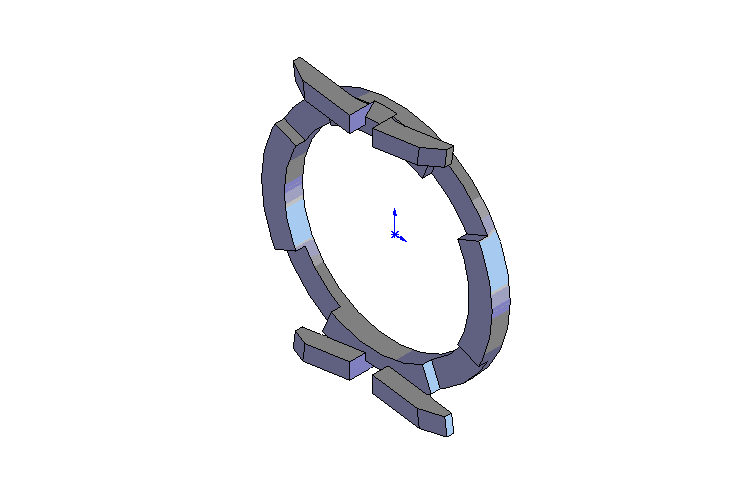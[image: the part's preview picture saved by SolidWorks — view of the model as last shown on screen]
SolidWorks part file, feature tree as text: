
SOLIDWORKS PART (.sldprt)
format: sldprt  version: not decoded by parser v0  size: 340,480 bytes
history: native  units: mm
features: plane x3, extrude x2, chamfer x2, material x1, sketch x1, cut_extrude x1, fillet x1 + 2 further entries (+10 scaffold rows collapsed)
feature tree (23):
  scaffold x10  (default folders/planes/origin — collapsed)
  material  "Matériau <non spécifié>"
  plane  "Plan de face"
  plane  "Plan de dessus"
  plane  "Plan de droite"
  sketch  "Esquisse1"  dims[D1=41.0mm D2=51.0mm]
  extrude  "Extrusion1"  Depth=4mm
  "Esquisse2"
  extrude  "Extrusion2"  Depth=3.5mm
  chamfer  "Chanfrein1"  Distance=2mm
  "Esquisse3"
  cut_extrude  "Enlèv. mat.-Extru.1"  Depth=2mm
  chamfer  "Chanfrein2"  Distance=2mm Angle=45deg
  fillet  "Congé1"  Radius=1mm
decode coverage: 7 of 7 modeling features carry decoded parameters; 2 rows unclassified (native names shown)
note: suppression state not decoded; provenance and decode notes live in map.json
